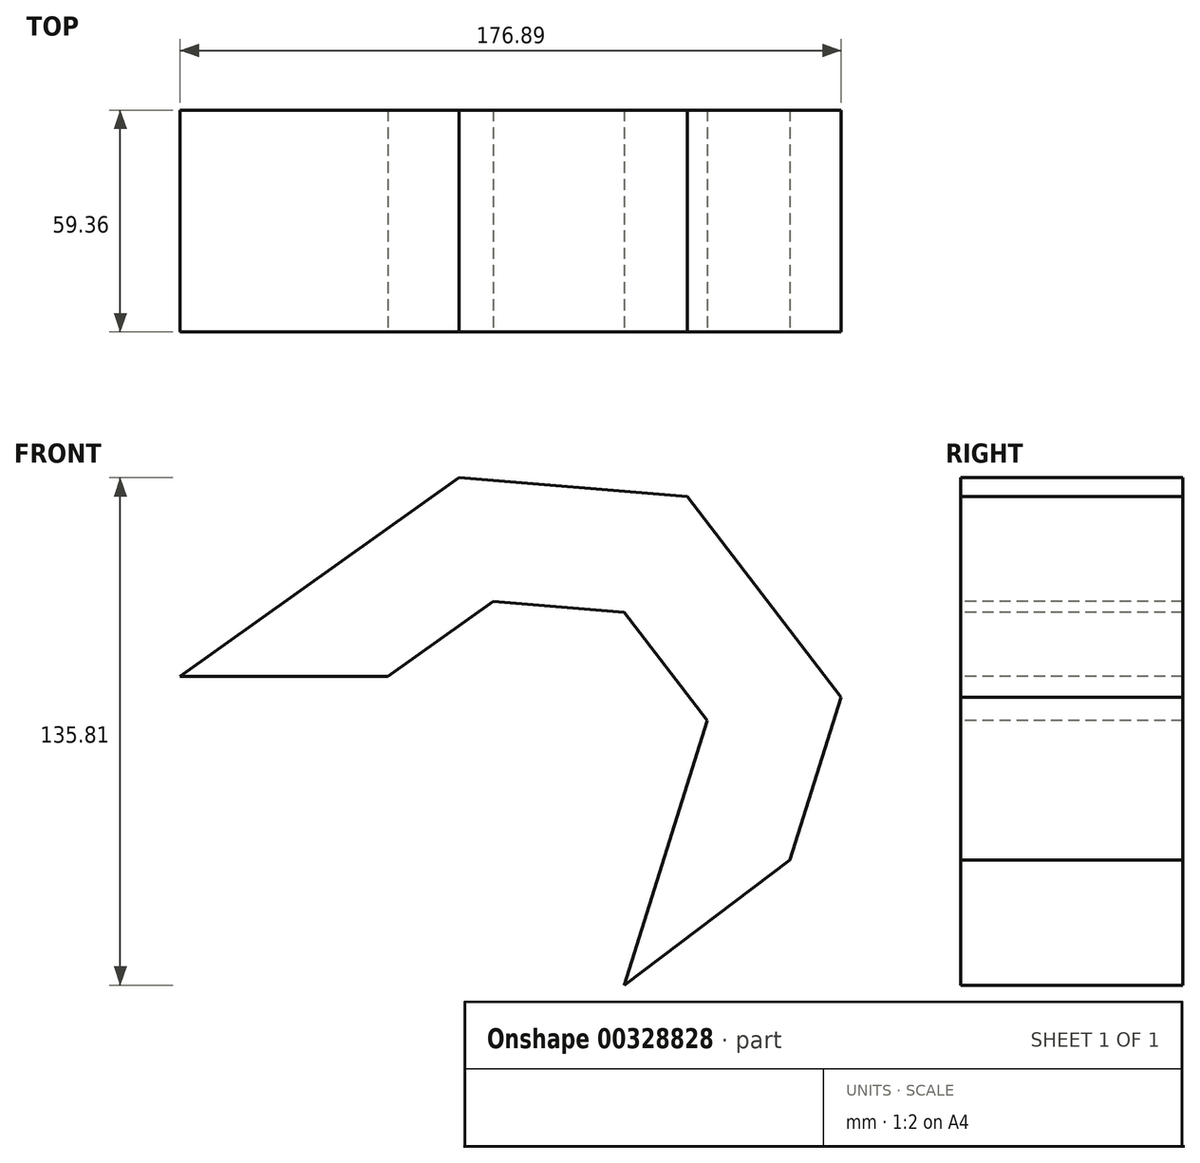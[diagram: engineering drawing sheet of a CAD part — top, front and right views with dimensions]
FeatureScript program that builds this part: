
annotation { "Feature Type Name" : "Feature", "Feature Type Description" : "" }
export const myFeature = defineFeature(function(context is Context, id is Id, definition is map)
    precondition{}
    {
        {
            var Q0;
            Q0=qCreatedBy(makeId("Top.planeOp"),FACE);
            var sketch = newSketch(context, id + "F0", { "sketchPlane" : qUnion([Q0])});
            skLineSegment(sketch, "E0.bottom", {"start": v(27.8, 29.68) * mm, "end": v(-27.8, 29.68) * mm});
            skLineSegment(sketch, "E0.top", {"start": v(27.8, -29.68) * mm, "end": v(-27.8, -29.68) * mm});
            skLineSegment(sketch, "E0.left", {"start": v(27.8, 29.68) * mm, "end": v(27.8, -29.68) * mm});
            skLineSegment(sketch, "E0.right", {"start": v(-27.8, 29.68) * mm, "end": v(-27.8, -29.68) * mm});
            skPoint(sketch, "E0.middle", {"position": v(0, 0) * mm});
            skSolve(sketch);
        }
        {
            var Q0;
            Q0=qCreatedBy(makeId("Front.planeOp"),FACE);
            var sketch = newSketch(context, id + "F1", { "sketchPlane" : qUnion([Q0])});
            skLineSegment(sketch, "E1", {"start": v(0, 0) * mm, "end": v(51.4, 36.58) * mm});
            skLineSegment(sketch, "E2", {"start": v(51.4, 36.58) * mm, "end": v(99.43, 32.58) * mm});
            skLineSegment(sketch, "E3", {"start": v(99.43, 32.58) * mm, "end": v(131.2, -8.75) * mm});
            skLineSegment(sketch, "E4", {"start": v(131.2, -8.75) * mm, "end": v(113.18, -65.92) * mm});
            skSolve(sketch);
        }
        {
            var Q0;
            Q0 = qSketchRegion(id + "F0", true);
            var Q1;
            Q1=sQuery(id+"F1.wireOp",EDGE,"E1");
            var Q2;
            Q2=sQuery(id+"F1.wireOp",EDGE,"E2");
            var Q3;
            Q3=sQuery(id+"F1.wireOp",EDGE,"E3");
            var Q4;
            Q4=sQuery(id+"F1.wireOp",EDGE,"E4");
            sweep(context, id + "F2", {"profiles" : qUnion([Q0]), "path" : qUnion([Q1, Q2, Q3, Q4])});
        }
    });
